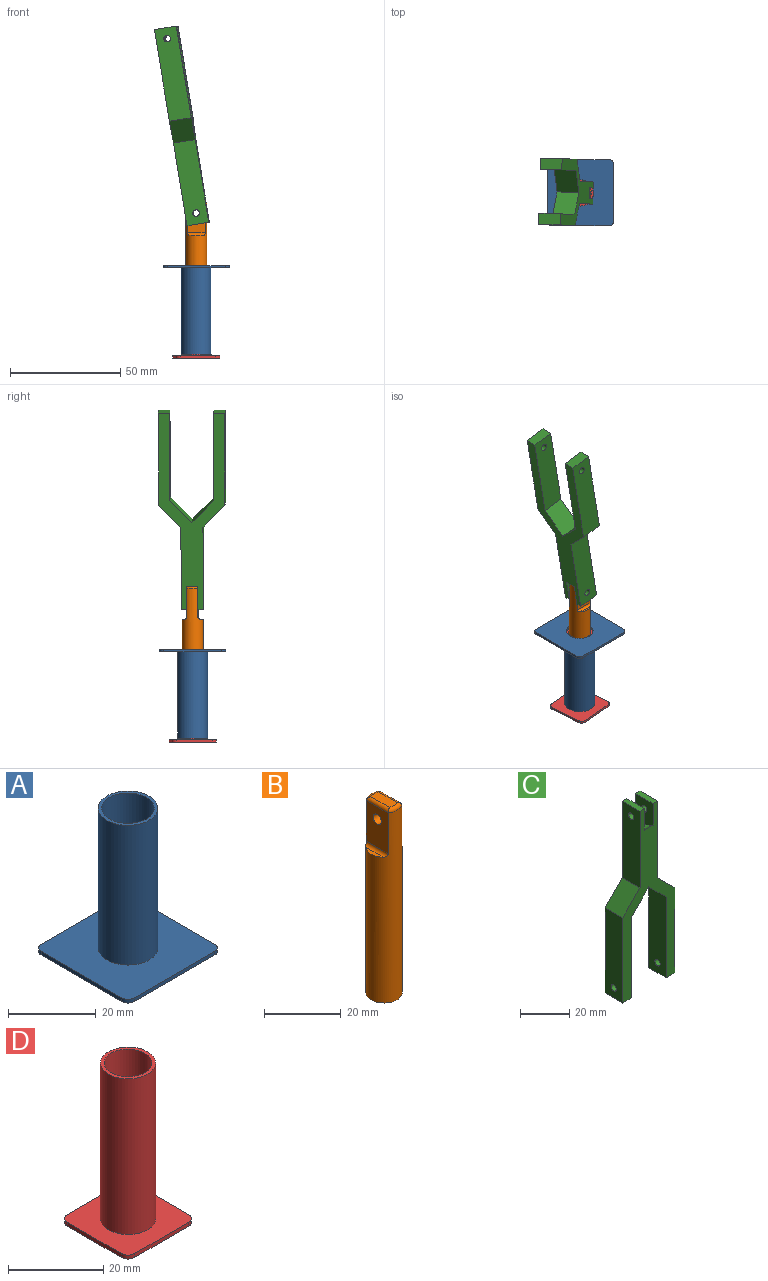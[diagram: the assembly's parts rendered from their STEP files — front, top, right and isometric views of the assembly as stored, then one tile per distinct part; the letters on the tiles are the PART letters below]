
ASSEMBLY  parts=4 mates=4
PART A: 13 faces, bbox 30x30x40 mm
  f0: plane 26x1mm, normal (1,0,0), area 26mm2, adj f1,f7,f8,f9
  f1: cylinder r=2mm len=2mm, axis (0,0,-1), area 3.1mm2, adj f0,f2,f8,f9
  f2: plane 26x1mm, normal (0,1,0), area 26mm2, adj f1,f3,f8,f9
  f3: cylinder r=2mm len=2mm, axis (0,0,-1), area 3.1mm2, adj f2,f4,f8,f9
  f4: plane 26x1mm, normal (-1,0,0), area 26mm2, adj f3,f5,f8,f9
  f5: cylinder r=2mm len=2mm, axis (0,0,-1), area 3.1mm2, adj f4,f6,f8,f9
  f6: plane 26x1mm, normal (0,-1,0), area 26mm2, adj f5,f7,f8,f9
  f7: cylinder r=2mm len=2mm, axis (0,0,-1), area 3.1mm2, adj f0,f6,f8,f9
  f8: plane 30x30mm, normal (0,0,1), area 751.3mm2, adj f0,f1,f2,f3,f4,f5,f6,f7
  f9: plane 30x30mm, normal (0,0,-1), area 783.5mm2, adj f0,f1,f2,f3,f4,f5,f6,f7
  f10: cylinder r=6mm len=40mm, axis (0,0,-1), area 1508mm2, adj f9,f12
  f11: cylinder r=6.8mm len=39mm, axis (0,0,-1), area 1666.3mm2, adj f8,f12
  f12: plane 13.6x13.6mm, normal (0,0,1), area 32.2mm2, adj f10,f11
PART B: 16 faces, bbox 9.5x10.3x61.5 mm
  f0: cylinder r=4.75mm len=60.5mm, axis (0,0,-1), area 1536.3mm2, adj f3,f5,f6,f7,f8,f10,f13,f14
  f1: plane 7.5x3mm, normal (0,0,1), area 21.9mm2, adj f10,f11,f12,f13
  f2: cylinder r=3.15mm len=45.5mm, axis (0,0,-1), area 900.5mm2, adj f3,f4
  f3: plane 9.5x9.5mm, normal (0,0,-1), area 39.7mm2, adj f0,f2
  f4: plane 6.3x6.3mm, normal (0,0,-1), area 31.2mm2, adj f2
  f5: plane 6.42x1.25mm, normal (0,0,1), area 5.5mm2, adj f0,f14
  f6: plane 13x8.08mm, normal (1,0,0), area 97.9mm2, adj f0,f9,f12,f14
  f7: plane 6.42x1.25mm, normal (0,0,1), area 5.5mm2, adj f0,f15
  f8: plane 13x8.08mm, normal (-1,0,0), area 97.9mm2, adj f0,f9,f11,f15
  f9: cylinder r=1.5mm len=5mm, axis (1,0,0), area 47.1mm2, adj f6,f8
  f10: torus R=3.75mm, axis (0,0,1), area 7mm2, adj f0,f1,f11,f12
  f11: cylinder r=1mm len=8.08mm, axis (0,-1,0), area 12mm2, adj f1,f8,f10,f13
  f12: cylinder r=1mm len=8.08mm, axis (0,1,0), area 12mm2, adj f1,f6,f10,f13
  f13: torus R=3.75mm, axis (0,0,1), area 7mm2, adj f0,f1,f11,f12
  f14: cylinder r=1mm len=8.08mm, axis (0,-1,0), area 11.8mm2, adj f0,f5,f6
  f15: cylinder r=1mm len=8.08mm, axis (0,1,0), area 11.8mm2, adj f0,f7,f8
PART C: 23 faces, bbox 30x10x90 mm
  f0: plane 10x2.5mm, normal (0,0,1), area 25mm2, adj f1,f2,f8,f17
  f1: plane 90x30mm, normal (0,-1,0), area 888.5mm2, adj f0,f3,f4,f5,f6,f7,f8,f9
  f2: plane 90x30mm, normal (0,1,0), area 888.5mm2, adj f0,f3,f4,f5,f6,f7,f8,f9
  f3: plane 42.07x10mm, normal (-1,0,0), area 413.6mm2, adj f1,f2,f4,f9,f20
  f4: plane 10x5mm, normal (0,0,-1), area 50mm2, adj f1,f2,f3,f5
  f5: plane 40x10mm, normal (1,0,0), area 392.9mm2, adj f1,f2,f4,f6,f20
  f6: plane 10x10mm, normal (0.71,0,-0.71), area 141.4mm2, adj f1,f2,f5,f13
  f7: plane 10x2.5mm, normal (0,0,1), area 25mm2, adj f1,f2,f14,f18
  f8: plane 37.93x10mm, normal (-1,0,0), area 372.2mm2, adj f0,f1,f2,f9,f22
  f9: plane 10x10mm, normal (-0.71,0,0.71), area 141.4mm2, adj f1,f2,f3,f8
  f10: plane 42.07x10mm, normal (1,0,0), area 413.6mm2, adj f1,f2,f11,f15,f19
  f11: plane 10x5mm, normal (0,0,-1), area 50mm2, adj f1,f2,f10,f12
  f12: plane 40x10mm, normal (-1,0,0), area 392.9mm2, adj f1,f2,f11,f13,f19
  f13: plane 10x10mm, normal (-0.71,0,-0.71), area 141.4mm2, adj f1,f2,f6,f12
  f14: plane 37.93x10mm, normal (1,0,0), area 372.2mm2, adj f1,f2,f7,f15,f21
  f15: plane 10x10mm, normal (0.71,0,0.71), area 141.4mm2, adj f1,f2,f10,f14
  f16: cylinder r=7.5mm len=10mm, axis (1,0,0), area 54.7mm2, adj f1,f2,f17,f18
  f17: plane 12.5x10mm, normal (1,0,0), area 111.9mm2, adj f0,f1,f2,f16,f22
  f18: plane 12.5x10mm, normal (-1,0,0), area 111.9mm2, adj f1,f2,f7,f16,f21
  f19: cylinder r=1.5mm len=5mm, axis (1,0,0), area 47.1mm2, adj f10,f12
  f20: cylinder r=1.5mm len=5mm, axis (1,0,0), area 47.1mm2, adj f3,f5
  f21: cylinder r=1.5mm len=3mm, axis (1,0,0), area 23.6mm2, adj f14,f18
  f22: cylinder r=1.5mm len=3mm, axis (1,0,0), area 23.6mm2, adj f8,f17
PART D: 13 faces, bbox 20x20x41 mm
  f0: plane 16x1mm, normal (1,0,0), area 16mm2, adj f1,f7,f8,f9
  f1: cylinder r=2mm len=2mm, axis (0,0,-1), area 3.1mm2, adj f0,f2,f8,f9
  f2: plane 16x1mm, normal (0,1,0), area 16mm2, adj f1,f3,f8,f9
  f3: cylinder r=2mm len=2mm, axis (0,0,-1), area 3.1mm2, adj f2,f4,f8,f9
  f4: plane 16x1mm, normal (-1,0,0), area 16mm2, adj f3,f5,f8,f9
  f5: cylinder r=2mm len=2mm, axis (0,0,-1), area 3.1mm2, adj f4,f6,f8,f9
  f6: plane 16x1mm, normal (0,-1,0), area 16mm2, adj f5,f7,f8,f9
  f7: cylinder r=2mm len=2mm, axis (0,0,-1), area 3.1mm2, adj f0,f6,f8,f9
  f8: plane 20x20mm, normal (0,0,1), area 290.9mm2, adj f0,f1,f2,f3,f4,f5,f6,f7
  f9: plane 20x20mm, normal (0,0,-1), area 318mm2, adj f0,f1,f2,f3,f4,f5,f6,f7
  f10: cylinder r=5mm len=41mm, axis (0,0,-1), area 1288.1mm2, adj f9,f12
  f11: cylinder r=5.8mm len=40mm, axis (0,0,-1), area 1457.7mm2, adj f8,f12
  f12: plane 11.6x11.6mm, normal (0,0,1), area 27.1mm2, adj f10,f11
PLACE A rot(axis=(0,1,0),180deg) t=(6.89,4.1,27.73)mm fixed
PLACE B rot(axis=(0,0,-1),91.6deg) t=(6.89,4.1,-4.97)mm fixed
PLACE C rot(axis=(-0.7,0.72,-0.06),173.6deg) t=(-11.66,4.62,134.63)mm
PLACE D rot(axis=(0,0,1),4.7deg) t=(6.89,4.1,-14.08)mm
MATE cylindrical A.f11 <-> D.f11  axis (0,0,1) through (6.89,4.1,7.23)mm
MATE cylindrical B.f0 <-> A.f11  axis (0,0,-1) through (6.89,4.1,25.28)mm
MATE planar C.f17 <-> B.f8  axis (-0.03,-1,0) through (6.8,6.6,52.54)mm
MATE cylindrical C.f16 <-> B.f9  axis (-0.03,-1,0) through (7,7.85,51.53)mm
